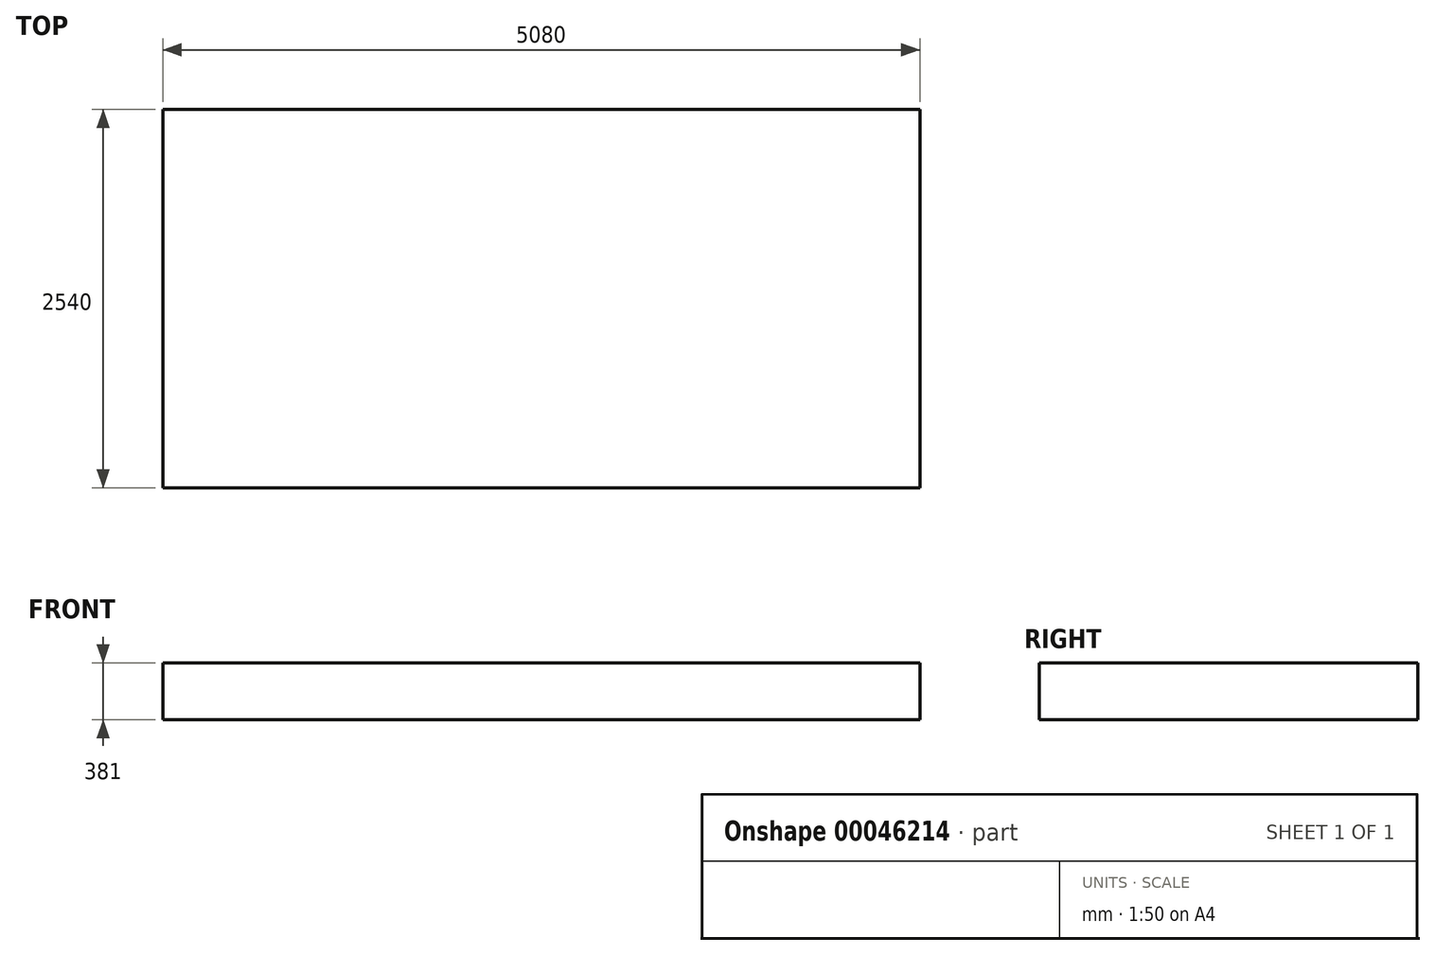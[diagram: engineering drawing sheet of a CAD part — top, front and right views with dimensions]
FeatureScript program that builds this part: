
annotation { "Feature Type Name" : "Feature", "Feature Type Description" : "" }
export const myFeature = defineFeature(function(context is Context, id is Id, definition is map)
    precondition{}
    {
        {
            var Q0;
            Q0=qCreatedBy(makeId("Top.planeOp"),FACE);
            var sketch = newSketch(context, id + "F0", { "sketchPlane" : qUnion([Q0])});
            skLineSegment(sketch, "E0.bottom", {"start": v(0, 0) * mm, "end": v(5080, 0) * mm});
            skLineSegment(sketch, "E0.top", {"start": v(0, 2540) * mm, "end": v(5080, 2540) * mm});
            skLineSegment(sketch, "E0.left", {"start": v(0, 0) * mm, "end": v(0, 2540) * mm});
            skLineSegment(sketch, "E0.right", {"start": v(5080, 0) * mm, "end": v(5080, 2540) * mm});
            skSolve(sketch);
        }
        {
            var Q0;
            Q0=makeQuery(id+"F0.imprint","IMPRINT",FACE,{"disambiguationData":[TD([[makeQuery(id+"F0.imprint","IMPRINT",EDGE,{"derivedFrom":sQuery(id+"F0.wireOp",EDGE,"E0.bottom")}),1.0]])]});
            extrude(context, id + "F1", {"entities" : qUnion([Q0]), "depth" : 381 * mm});
        }
    });
